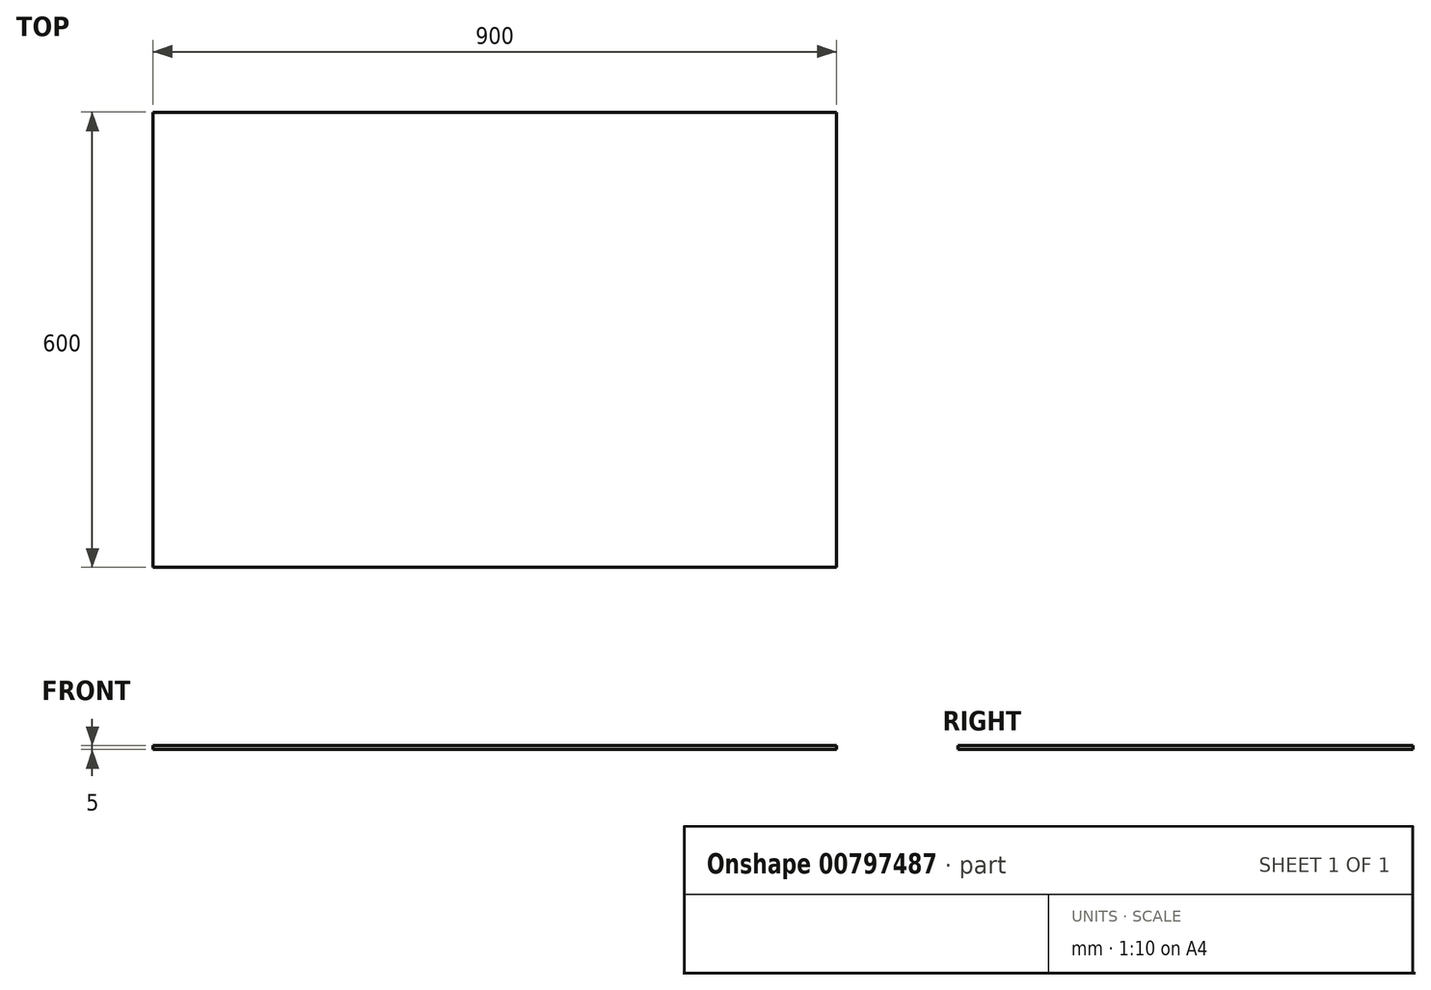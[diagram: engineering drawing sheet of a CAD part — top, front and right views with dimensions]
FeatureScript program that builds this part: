
annotation { "Feature Type Name" : "Feature", "Feature Type Description" : "" }
export const myFeature = defineFeature(function(context is Context, id is Id, definition is map)
    precondition{}
    {
        {
            var Q0;
            Q0=qCreatedBy(makeId("Top.planeOp"),FACE);
            var sketch = newSketch(context, id + "F0", { "sketchPlane" : qUnion([Q0])});
            skLineSegment(sketch, "E0.bottom", {"start": v(-479.92, -295.77) * mm, "end": v(420.08, -295.77) * mm});
            skLineSegment(sketch, "E0.top", {"start": v(-479.92, 304.23) * mm, "end": v(420.08, 304.23) * mm});
            skLineSegment(sketch, "E0.left", {"start": v(-479.92, -295.77) * mm, "end": v(-479.92, 304.23) * mm});
            skLineSegment(sketch, "E0.right", {"start": v(420.08, -295.77) * mm, "end": v(420.08, 304.23) * mm});
            skSolve(sketch);
        }
        {
            var Q0;
            Q0=makeQuery(id+"F0.imprint","IMPRINT",FACE,{"disambiguationData":[TD([[makeQuery(id+"F0.imprint","IMPRINT",EDGE,{"derivedFrom":sQuery(id+"F0.wireOp",EDGE,"E0.bottom")}),1.0]])]});
            extrude(context, id + "F1", {"entities" : qUnion([Q0]), "depth" : 5 * mm, "offsetDistance" : 25 * mm});
        }
    });
